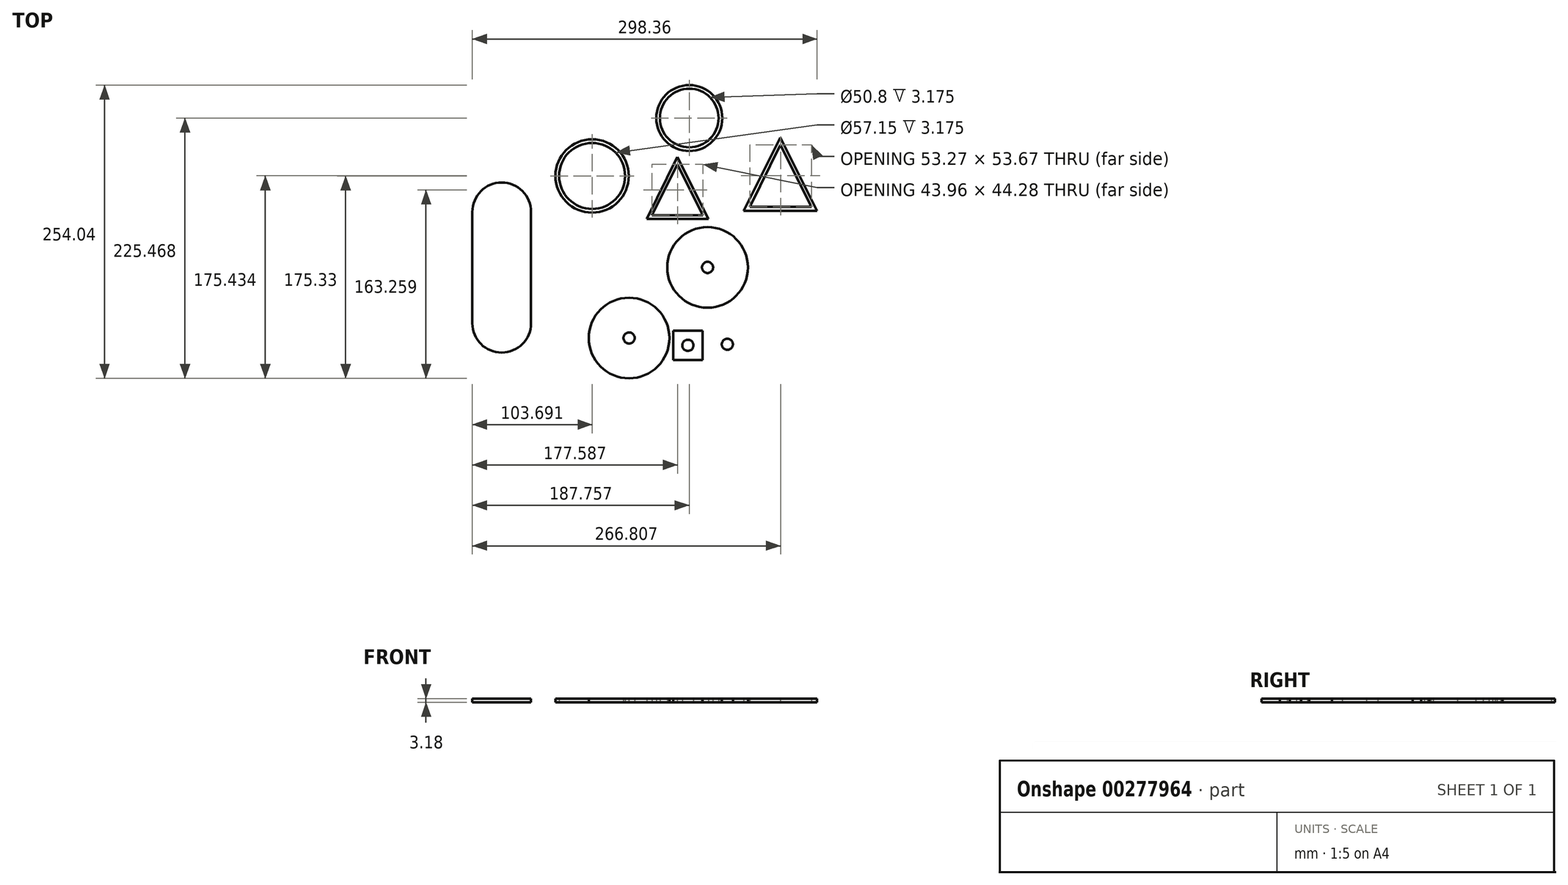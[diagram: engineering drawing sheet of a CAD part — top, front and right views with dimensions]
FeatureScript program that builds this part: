
annotation { "Feature Type Name" : "Feature", "Feature Type Description" : "" }
export const myFeature = defineFeature(function(context is Context, id is Id, definition is map)
    precondition{}
    {
        {
            var Q0;
            Q0=qCreatedBy(makeId("Top.planeOp"),FACE);
            var sketch = newSketch(context, id + "F0", { "sketchPlane" : qUnion([Q0])});
            skLineSegment(sketch, "E0", {"start": v(57.75, 2.39) * mm, "end": v(121.25, 2.39) * mm});
            skLineSegment(sketch, "E1", {"start": v(57.75, 2.39) * mm, "end": v(89.5, 65.89) * mm});
            skLineSegment(sketch, "E2", {"start": v(89.5, 65.89) * mm, "end": v(121.25, 2.39) * mm});
            skCircle(sketch, "E3", {"center": v(-73.42, 32.6) * mm, "radius": 31.75 * mm});
            skCircle(sketch, "E4", {"center": v(-73.42, 32.6) * mm, "radius": 28.58 * mm});
            skLineSegment(sketch, "E5", {"start": v(63.06, 5.87) * mm, "end": v(89.5, 59.54) * mm});
            skLineSegment(sketch, "E6", {"start": v(63.06, 5.87) * mm, "end": v(116.33, 5.87) * mm});
            skLineSegment(sketch, "E7", {"start": v(89.5, 59.54) * mm, "end": v(116.33, 5.87) * mm});
            skSolve(sketch);
        }
        {
            var Q0;
            Q0=qCreatedBy(makeId("Top.planeOp"),FACE);
            var sketch = newSketch(context, id + "F1", { "sketchPlane" : qUnion([Q0])});
            skCircle(sketch, "E8", {"center": v(-41.46, -107.8) * mm, "radius": 34.93 * mm});
            skCircle(sketch, "E9", {"center": v(-41.46, -107.8) * mm, "radius": 4.83 * mm});
            skSolve(sketch);
        }
        {
            var Q0;
            Q0=makeQuery(id+"F1.imprint","IMPRINT",FACE,{"disambiguationData":[TD([[makeQuery(id+"F1.imprint","IMPRINT",EDGE,{"derivedFrom":sQuery(id+"F1.wireOp",EDGE,"E8")}),1.0]])]});
            extrude(context, id + "F2", {"entities" : qUnion([Q0]), "depth" : 3.17 * mm});
        }
        {
            var Q0;
            Q0=qCreatedBy(makeId("Top.planeOp"),FACE);
            var sketch = newSketch(context, id + "F3", { "sketchPlane" : qUnion([Q0])});
            skCircle(sketch, "E10", {"center": v(26.47, -46.67) * mm, "radius": 34.93 * mm});
            skSolve(sketch);
        }
        {
            var Q0;
            Q0=makeQuery(id+"F3.imprint","IMPRINT",FACE,{"disambiguationData":[TD([[makeQuery(id+"F3.imprint","IMPRINT",EDGE,{"derivedFrom":sQuery(id+"F3.wireOp",EDGE,"E10")}),1.0]])]});
            extrude(context, id + "F4", {"entities" : qUnion([Q0]), "depth" : 3.17 * mm});
        }
        {
            var Q0;
            Q0=makeQuery(id+"F4.opExtrude","CAP_FACE",FACE,{"disambiguationData":[OSD([sQuery(id+"F3.wireOp",EDGE,"E10")])],"isStart":false});
            var sketch = newSketch(context, id + "F5", { "sketchPlane" : qUnion([Q0])});
            skPoint(sketch, "E11", {"position": v(26.47, -46.67) * mm});
            skCircle(sketch, "E12", {"center": v(26.47, -46.67) * mm, "radius": 4.83 * mm});
            skSolve(sketch);
        }
        {
            var Q0;
            Q0=makeQuery(id+"F5.imprint","IMPRINT",FACE,{"disambiguationData":[TD([[makeQuery(id+"F5.imprint","IMPRINT",EDGE,{"derivedFrom":sQuery(id+"F5.wireOp",EDGE,"E12")}),1.0]])]});
            extrude(context, id + "F6", {"entities" : qUnion([Q0]), "operationType" : NewBodyOperationType.REMOVE, "oppositeDirection" : true, "depth" : 25.4 * mm});
        }
        {
            var Q0;
            Q0=qCreatedBy(makeId("Top.planeOp"),FACE);
            var sketch = newSketch(context, id + "F7", { "sketchPlane" : qUnion([Q0])});
            skLineSegment(sketch, "E13.bottom", {"start": v(-3.27, -101.45) * mm, "end": v(22.13, -101.45) * mm});
            skLineSegment(sketch, "E13.top", {"start": v(-3.27, -126.85) * mm, "end": v(22.13, -126.85) * mm});
            skLineSegment(sketch, "E13.left", {"start": v(-3.27, -101.45) * mm, "end": v(-3.27, -126.85) * mm});
            skLineSegment(sketch, "E13.right", {"start": v(22.13, -101.45) * mm, "end": v(22.13, -126.85) * mm});
            skPoint(sketch, "E14", {"position": v(9.43, -114.15) * mm});
            skCircle(sketch, "E15", {"center": v(9.43, -114.15) * mm, "radius": 4.83 * mm});
            skCircle(sketch, "E16.MirrorC", {"center": v(43.62, -113.25) * mm, "radius": 4.83 * mm});
            skLineSegment(sketch, "E17.MirrorCS", {"start": v(30.02, -99.66) * mm, "end": v(30.02, -125.06) * mm});
            skLineSegment(sketch, "E18.MirrorCS", {"start": v(55.42, -99.66) * mm, "end": v(30.02, -99.66) * mm});
            skLineSegment(sketch, "E19.MirrorCS", {"start": v(55.42, -125.06) * mm, "end": v(30.02, -125.06) * mm});
            skLineSegment(sketch, "E20.MirrorCS", {"start": v(55.42, -99.66) * mm, "end": v(55.42, -125.06) * mm});
            skSolve(sketch);
        }
        {
            var Q0;
            Q0=makeQuery(id+"F7.imprint","IMPRINT",FACE,{"disambiguationData":[TD([[makeQuery(id+"F7.imprint","IMPRINT",EDGE,{"derivedFrom":sQuery(id+"F7.wireOp",EDGE,"E13.bottom")}),-1.0]])]});
            var Q1;
            Q1=makeQuery(id+"F7.imprint","IMPRINT",FACE,{"disambiguationData":[TD([[makeQuery(id+"F7.imprint","IMPRINT",EDGE,{"derivedFrom":sQuery(id+"F7.wireOp",EDGE,"xvH5cVz1-pj4Y-tES7-m2WN-IS9xY6hBvVlf.bottom")}),-1.0]])]});
            var Q2;
            Q2=makeQuery(id+"F7.imprint","IMPRINT",FACE,{"disambiguationData":[TD([[makeQuery(id+"F7.imprint","IMPRINT",EDGE,{"derivedFrom":sQuery(id+"F7.wireOp",EDGE,"E16.MirrorC")}),1.0]])]});
            extrude(context, id + "F8", {"entities" : qUnion([Q0, Q1, Q2]), "depth" : 3.17 * mm});
        }
        {
            var Q0;
            Q0=makeQuery(id+"F0.imprint","IMPRINT",FACE,{"disambiguationData":[TD([[makeQuery(id+"F0.imprint","IMPRINT",EDGE,{"derivedFrom":sQuery(id+"F0.wireOp",EDGE,"UoLDU8TW-Y7RX-MBZK-CyKg-IxwF9U3ngnjX")}),1.0]])]});
            var Q1;
            Q1=makeQuery(id+"F0.imprint","IMPRINT",FACE,{"disambiguationData":[TD([[makeQuery(id+"F0.imprint","IMPRINT",EDGE,{"derivedFrom":sQuery(id+"F0.wireOp",EDGE,"E3")}),1.0]])]});
            var Q2;
            Q2=makeQuery(id+"F0.imprint","IMPRINT",FACE,{"disambiguationData":[TD([[makeQuery(id+"F0.imprint","IMPRINT",EDGE,{"derivedFrom":sQuery(id+"F0.wireOp",EDGE,"E0")}),1.0]])]});
            var Q3;
            Q3=makeQuery(id+"F0.imprint","IMPRINT",FACE,{"disambiguationData":[TD([[makeQuery(id+"F0.imprint","IMPRINT",EDGE,{"derivedFrom":sQuery(id+"F0.wireOp",EDGE,"p5byj5YM-fA1L-J3r7-5kZM-NJmz9XegK4rt")}),1.0]])]});
            extrude(context, id + "F9", {"entities" : qUnion([Q0, Q1, Q2, Q3]), "depth" : 3.17 * mm});
        }
        {
            var Q0;
            Q0=qCreatedBy(makeId("Top.planeOp"),FACE);
            var sketch = newSketch(context, id + "F10", { "sketchPlane" : qUnion([Q0])});
            skArc(sketch, "E21", {"start": v(-126.31, 1.47) * mm, "mid": v(-151.71, 26.87) * mm, "end": v(-177.11, 1.47) * mm});
            skLineSegment(sketch, "E22", {"start": v(-177.11, 1.47) * mm, "end": v(-177.11, -95.05) * mm});
            skArc(sketch, "E23", {"start": v(-177.11, -95.05) * mm, "mid": v(-151.71, -120.45) * mm, "end": v(-126.31, -95.05) * mm});
            skLineSegment(sketch, "E24", {"start": v(-126.31, 1.47) * mm, "end": v(-126.31, -95.05) * mm});
            skSolve(sketch);
        }
        {
            var Q0;
            Q0=makeQuery(id+"F10.imprint","IMPRINT",FACE,{"disambiguationData":[TD([[makeQuery(id+"F10.imprint","IMPRINT",EDGE,{"derivedFrom":sQuery(id+"F10.wireOp",EDGE,"E21")}),1.0]])]});
            extrude(context, id + "F11", {"entities" : qUnion([Q0]), "depth" : 3.17 * mm});
        }
        {
            var Q0;
            Q0=qCreatedBy(makeId("Top.planeOp"),FACE);
            var sketch = newSketch(context, id + "F12", { "sketchPlane" : qUnion([Q0])});
            skLineSegment(sketch, "E25", {"start": v(-26.13, -4.65) * mm, "end": v(0.31, 49.02) * mm});
            skLineSegment(sketch, "E26", {"start": v(-26.13, -4.65) * mm, "end": v(27.15, -4.65) * mm});
            skLineSegment(sketch, "E27", {"start": v(0.31, 49.02) * mm, "end": v(27.15, -4.65) * mm});
            skLineSegment(sketch, "E28", {"start": v(0.31, 42.67) * mm, "end": v(22.46, -1.61) * mm});
            skLineSegment(sketch, "E29", {"start": v(0.31, 42.67) * mm, "end": v(-21.5, -1.61) * mm});
            skLineSegment(sketch, "E30", {"start": v(-21.5, -1.61) * mm, "end": v(22.46, -1.61) * mm});
            skSolve(sketch);
        }
        {
            var Q0;
            Q0=makeQuery(id+"F12.imprint","IMPRINT",FACE,{"disambiguationData":[TD([[makeQuery(id+"F12.imprint","IMPRINT",EDGE,{"derivedFrom":sQuery(id+"F12.wireOp",EDGE,"E25")}),-1.0]])]});
            extrude(context, id + "F13", {"entities" : qUnion([Q0]), "depth" : 3.17 * mm});
        }
        {
            var Q0;
            Q0=qCreatedBy(makeId("Top.planeOp"),FACE);
            var sketch = newSketch(context, id + "F14", { "sketchPlane" : qUnion([Q0])});
            skCircle(sketch, "E31", {"center": v(10.65, 82.74) * mm, "radius": 28.58 * mm});
            skCircle(sketch, "E32", {"center": v(10.65, 82.74) * mm, "radius": 25.4 * mm});
            skSolve(sketch);
        }
        {
            var Q0;
            Q0=makeQuery(id+"F14.imprint","IMPRINT",FACE,{"disambiguationData":[TD([[makeQuery(id+"F14.imprint","IMPRINT",EDGE,{"derivedFrom":sQuery(id+"F14.wireOp",EDGE,"E31")}),1.0]])]});
            extrude(context, id + "F15", {"entities" : qUnion([Q0]), "depth" : 3.17 * mm});
        }
    });
